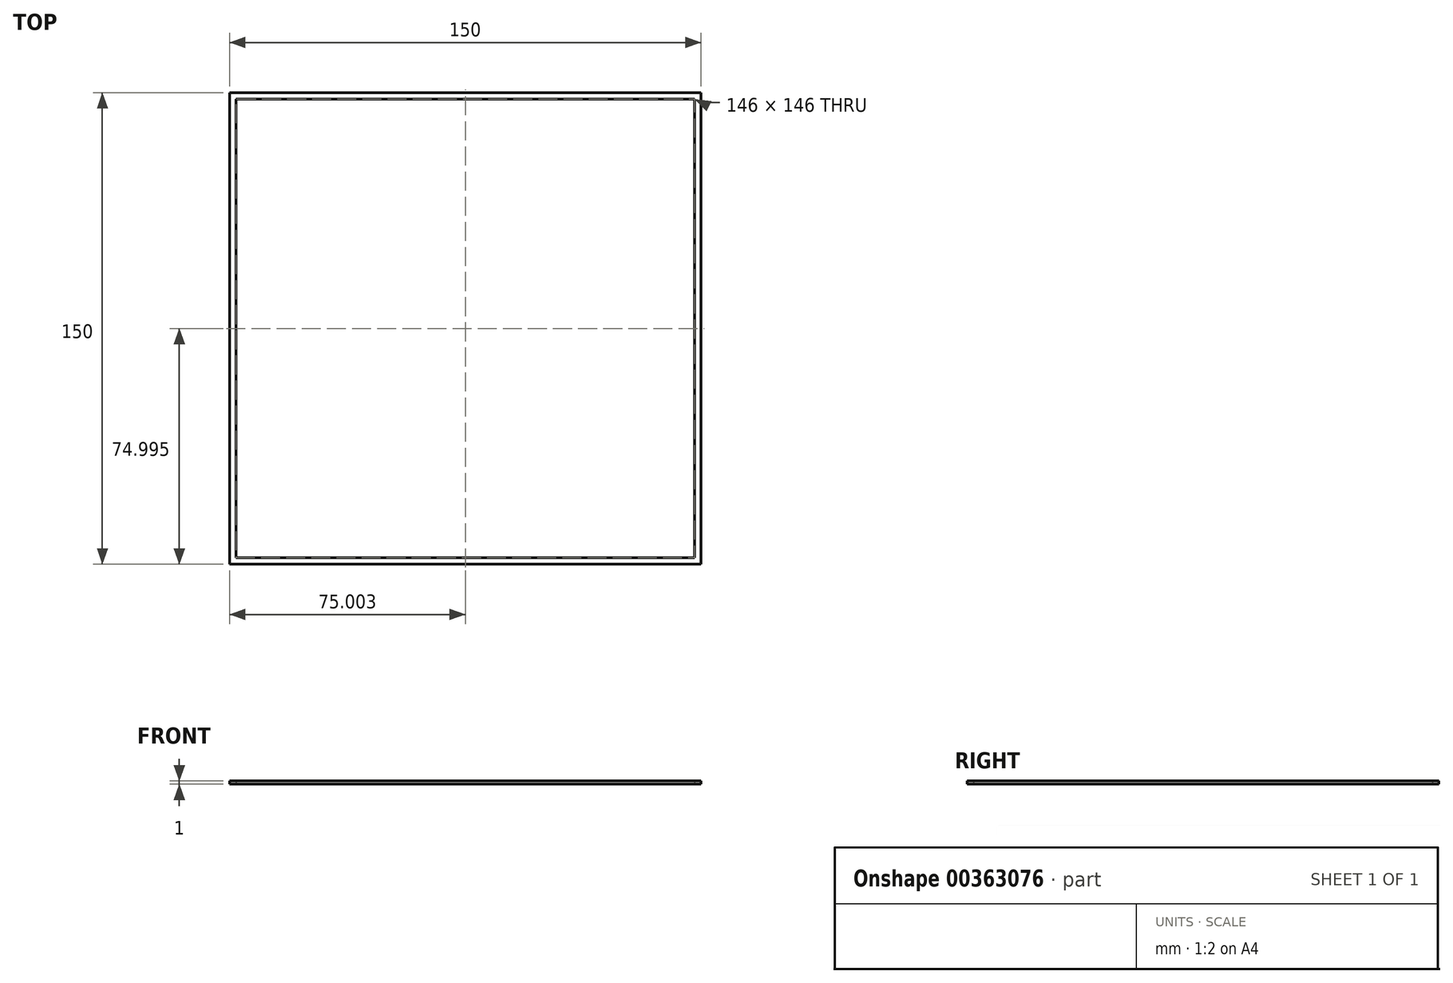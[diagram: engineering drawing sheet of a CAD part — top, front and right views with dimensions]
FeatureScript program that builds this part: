
annotation { "Feature Type Name" : "Feature", "Feature Type Description" : "" }
export const myFeature = defineFeature(function(context is Context, id is Id, definition is map)
    precondition{}
    {
        {
            var Q0;
            Q0=qCreatedBy(makeId("Top.planeOp"),FACE);
            var sketch = newSketch(context, id + "F0", { "sketchPlane" : qUnion([Q0])});
            skLineSegment(sketch, "E0.bottom", {"start": v(-22.47, 147.13) * mm, "end": v(127.53, 147.13) * mm});
            skLineSegment(sketch, "E0.top", {"start": v(-22.47, -2.87) * mm, "end": v(127.53, -2.87) * mm});
            skLineSegment(sketch, "E0.left", {"start": v(-22.47, 147.13) * mm, "end": v(-22.47, -2.87) * mm});
            skLineSegment(sketch, "E0.right", {"start": v(127.53, 147.13) * mm, "end": v(127.53, -2.87) * mm});
            skLineSegment(sketch, "E1.0", {"start": v(-20.47, 145.13) * mm, "end": v(125.53, 145.13) * mm});
            skLineSegment(sketch, "E1.1", {"start": v(-20.47, 145.13) * mm, "end": v(-20.47, -0.87) * mm});
            skLineSegment(sketch, "E1.2", {"start": v(-20.47, -0.87) * mm, "end": v(125.53, -0.87) * mm});
            skLineSegment(sketch, "E1.3", {"start": v(125.53, 145.13) * mm, "end": v(125.53, -0.87) * mm});
            skSolve(sketch);
        }
        {
            var Q0;
            Q0=makeQuery(id+"F0.imprint","IMPRINT",FACE,{"disambiguationData":[TD([[makeQuery(id+"F0.imprint","IMPRINT",EDGE,{"derivedFrom":sQuery(id+"F0.wireOp",EDGE,"E0.bottom")}),-1.0]])]});
            extrude(context, id + "F1", {"entities" : qUnion([Q0]), "depth" : 1 * mm});
        }
    });
